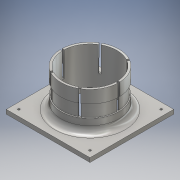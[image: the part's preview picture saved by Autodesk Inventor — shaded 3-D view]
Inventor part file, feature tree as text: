
AUTODESK INVENTOR PART (.ipt)
format: ipt  version: 2016 (Build 200138000, 138)  size: 209,408 bytes
history: native  units: mm
features: extrude x4, sketch x4, projected_geometry x2, plane x1, pattern_circular x1, fillet x1, reference x1
ambient origin geometry x8: Origin, YZ Plane, XZ Plane, XY Plane, X Axis, Y Axis, Z Axis, Center Point
bodies: Solid1 (feature_tree)
feature tree (14):
  extrude  "Extrusion1"  TaperAngle=0.0deg  [1 undecoded]
  extrude  "Extrusion2"  Depth=77.0mm
  plane  "Work Plane1"
  extrude  "Extrusion3"  Depth=54.0mm
  extrude  "Extrusion4"  [1 undecoded]
  pattern_circular  "Circular Pattern1"  [2 undecoded]
  fillet  "Fillet1"  Radius=18.0mm
  sketch  "Sketch1"  dims[d0=6.0mm d1=0.0mm]
  reference  "Reference1"
  sketch  "Sketch3"  dims[d3=75.0mm d4=77.0mm]
  sketch  "Sketch4"  dims[d5=3.0mm d6=54.0mm]
  sketch  "Sketch5"  dims[d7=0.0mm d8=-36.0mm d9=1.5mm d10=18.0mm d11=0.0mm d12=0.698132mm d13=0.0mm d14=0.0mm d15=60.0mm d16=360.0deg d18=9.0mm]
  projected_geometry  "Projected Loop1"
  projected_geometry  "Project Cut Edges1"
note: 4 required parameter values undecoded (feature->parameter linkage not recoverable at this tier; creation-order binding heuristic only, values carry confidence <= 0.55)
